# Revit family: Drinking_Fountain-Haws_Corporation-Wall_Mounted_1001 new new
name_source: partatom
category: Plumbing Fixtures
revit_build: Autodesk Revit Architecture 2015 (Build: 20160512_1515(x64)
units: mm (PartAtom-declared; Revit-internal decimal feet)

## types (6) — shared parameters
Assembly Code = D2010810
Back Panel Width = 1' - 3"
Bowl Diameter = 1' - 2 1/8"
Cost Note = For Cost information please visit the Resource tab in the Product Page URL
Default Elevation = 2' - 3"
Flow = 0 GPM
HW Connection = No
Keynote = 15410.A1
Manufacturer = Haws Corporation
Product Documentation Link = https://www.hawsco.com
Product Page URL = http://www.hawsco.com
Sanitary Radius = 0' - 0 5/8"
Series = The Haws 1001 barrier-free drinking fountain
Supply Radius = 0' - 0 3/16"
Tubing = Metal - Haws Corporation - Copper
URL = http://www.hawsco.com
Vent Connection = Yes
Version = 2014-v2.0a
Waste Level = 2' - 4 3/32"
zero-valued in all types: Cost, HWFU, WFU

## per-type parameters (varying)
| type | Back Plate | Bowl | Bracket | CW Connection | CWFU | Description | Pipe Offset | Type Comments | Waste Connection |
| 1001HPSBP | Metal - Haws Corporation - High Polished Stainless Steel | Metal - Haws Corporation - High Polished Stainless Steel | Metal - Haws Corporation - High Polished Stainless Steel | Yes | 2 | Wall Mounted Drinking Fountain with backwall access of plumbing | 1' - 0 1/2" | Design with a high-polished stainless steel finish and back panel | No |
| 1001HPS | Metal - Haws Corporation - High Polished Stainless Steel | Metal - Haws Corporation - High Polished Stainless Steel | Metal - Haws Corporation - High Polished Stainless Steel | No | 1 | Wall Mounted Drinking Fountain with backwall access of plumbing | 1' - 0 1/2" | Design with a high-polished stainless steel finish | No |
| 1001 | Metal - Haws Corporation - Satin Stainless Steel | Metal - Haws Corporation - Satin Stainless Steel | Metal - Haws Corporation - Satin Stainless Steel | No | 1 | Wall Mounted Drinking Fountain with backwall access of plumbing | 1' - 0 1/2" | No supplied back panel | No |
| 1001HPSMS | Metal - Haws Corporation - High Polished Stainless Steel | Metal - Haws Corporation - High Polished Stainless Steel | Metal - Haws Corporation - High Polished Stainless Steel | Yes | 3 | Wall Mounted Drinking Fountain with front access of plumbing | 0' - 3" | Design with a high-polished stainless steel finish and front access of plumbing | Yes |
| 1001BP | Metal - Haws Corporation - Satin Stainless Steel | Metal - Haws Corporation - Satin Stainless Steel | Metal - Haws Corporation - Satin Stainless Steel | Yes | 2 | Wall Mounted Drinking Fountain with backwall access of plumbing | 1' - 0 1/2" | Design with supplied back panel | No |
| 1001MS | Metal - Haws Corporation - Satin Stainless Steel | Metal - Haws Corporation - Satin Stainless Steel | Metal - Haws Corporation - Satin Stainless Steel | Yes | 3 | Wall Mounted Drinking Fountain with front access of plumbing | 0' - 3" | MS (mounting system) allows for front access of plumbing | Yes |

note: column(s) folded — value = type name in every type: Model

## geometry (parser evidence)
native form markers: Blend x30, Sweep x2
no freeform markers — native parametric forms only
